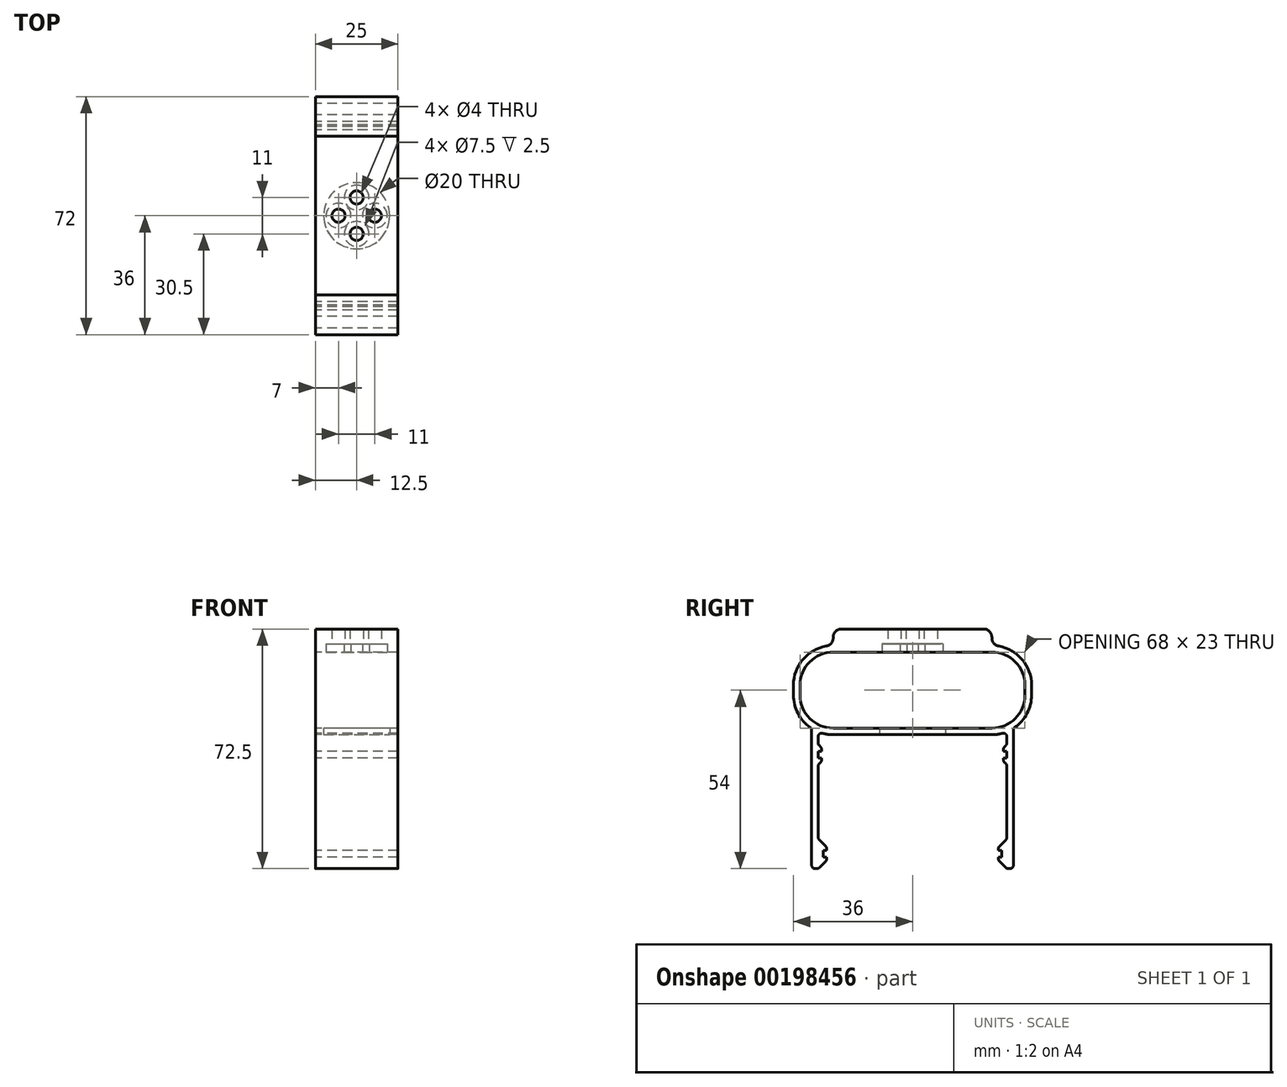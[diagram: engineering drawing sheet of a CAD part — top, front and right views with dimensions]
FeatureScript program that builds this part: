
annotation { "Feature Type Name" : "Feature", "Feature Type Description" : "" }
export const myFeature = defineFeature(function(context is Context, id is Id, definition is map)
    precondition{}
    {
        {
            var Q0;
            Q0=qCreatedBy(makeId("Right.planeOp"),FACE);
            var sketch = newSketch(context, id + "F0", { "sketchPlane" : qUnion([Q0])});
            skLineSegment(sketch, "E0.bottom", {"start": v(-24, 0) * mm, "end": v(24, 0) * mm});
            skLineSegment(sketch, "E0.top", {"start": v(-24, 23) * mm, "end": v(24, 23) * mm});
            skLineSegment(sketch, "E0.left", {"start": v(-34, 10) * mm, "end": v(-34, 13) * mm});
            skLineSegment(sketch, "E0.right", {"start": v(34, 10) * mm, "end": v(34, 13) * mm});
            skPoint(sketch, "E1.visualSharp", {"position": v(-34, 23) * mm});
            skArc(sketch, "E1.filletArc", {"start": v(-24, 23) * mm, "mid": v(-31.07, 20.07) * mm, "end": v(-34, 13) * mm});
            skPoint(sketch, "E2.visualSharp", {"position": v(-34, 0) * mm});
            skArc(sketch, "E2.filletArc", {"start": v(-34, 10) * mm, "mid": v(-31.07, 2.93) * mm, "end": v(-24, 0) * mm});
            skArc(sketch, "E3.filletArc", {"start": v(24, 0) * mm, "mid": v(31.07, 2.93) * mm, "end": v(34, 10) * mm});
            skPoint(sketch, "E4.visualSharp", {"position": v(34, 23) * mm});
            skArc(sketch, "E4.filletArc", {"start": v(34, 13) * mm, "mid": v(31.07, 20.07) * mm, "end": v(24, 23) * mm});
            skLineSegment(sketch, "E5.0", {"start": v(-24, 25) * mm, "end": v(24, 25) * mm});
            skArc(sketch, "E5.1", {"start": v(36, 13) * mm, "mid": v(32.49, 21.49) * mm, "end": v(24, 25) * mm});
            skArc(sketch, "E5.2", {"start": v(-24, 25) * mm, "mid": v(-32.49, 21.49) * mm, "end": v(-36, 13) * mm});
            skLineSegment(sketch, "E5.3", {"start": v(36, 10) * mm, "end": v(36, 13) * mm});
            skLineSegment(sketch, "E5.4", {"start": v(-36, 10) * mm, "end": v(-36, 13) * mm});
            skArc(sketch, "E5.5", {"start": v(-36, 10) * mm, "mid": v(-34.66, 4.48) * mm, "end": v(-30.92, 0.2) * mm});
            skLineSegment(sketch, "E5.6", {"start": v(-24, -2) * mm, "end": v(24, -2) * mm});
            skArc(sketch, "E5.7", {"start": v(24, -2) * mm, "mid": v(25.63, -1.89) * mm, "end": v(27.23, -1.56) * mm});
            skLineSegment(sketch, "E6", {"start": v(-28.5, -2.52) * mm, "end": v(-28.5, -4.59) * mm});
            skLineSegment(sketch, "E7", {"start": v(-28.2, -5.3) * mm, "end": v(-27.8, -5.7) * mm});
            skLineSegment(sketch, "E8", {"start": v(-27.5, -6.41) * mm, "end": v(-27.5, -7) * mm});
            skLineSegment(sketch, "E9", {"start": v(-27.5, -7) * mm, "end": v(-28.5, -7) * mm});
            skLineSegment(sketch, "E10", {"start": v(-28.5, -7) * mm, "end": v(-28.5, -9) * mm});
            skLineSegment(sketch, "E11", {"start": v(-28.5, -9) * mm, "end": v(-27.5, -9) * mm});
            skLineSegment(sketch, "E12", {"start": v(-27.5, -9) * mm, "end": v(-27.5, -9.59) * mm});
            skLineSegment(sketch, "E13", {"start": v(-27.8, -10.3) * mm, "end": v(-28.2, -10.7) * mm});
            skLineSegment(sketch, "E14", {"start": v(-28.5, -11.41) * mm, "end": v(-28.5, -33.09) * mm});
            skLineSegment(sketch, "E15", {"start": v(-28.2, -33.8) * mm, "end": v(-26.3, -35.7) * mm});
            skLineSegment(sketch, "E16", {"start": v(-26, -36.41) * mm, "end": v(-26, -37) * mm});
            skLineSegment(sketch, "E17", {"start": v(-26, -37) * mm, "end": v(-27, -37) * mm});
            skLineSegment(sketch, "E18", {"start": v(-27, -37) * mm, "end": v(-27, -39) * mm});
            skLineSegment(sketch, "E19", {"start": v(-27, -39) * mm, "end": v(-26, -39) * mm});
            skLineSegment(sketch, "E20", {"start": v(-26, -39) * mm, "end": v(-26, -39.59) * mm});
            skLineSegment(sketch, "E21", {"start": v(-26.3, -40.3) * mm, "end": v(-28.2, -42.2) * mm});
            skLineSegment(sketch, "E22", {"start": v(-28.91, -42.5) * mm, "end": v(-29.5, -42.5) * mm});
            skLineSegment(sketch, "E23", {"start": v(-30.5, -41.5) * mm, "end": v(-30.5, -0.62) * mm});
            skLineSegment(sketch, "E24.MirrorCS", {"start": v(30.5, -41.5) * mm, "end": v(30.5, -0.62) * mm});
            skLineSegment(sketch, "E25.MirrorCS", {"start": v(28.5, -2.52) * mm, "end": v(28.5, -4.59) * mm});
            skLineSegment(sketch, "E26.MirrorCS", {"start": v(28.2, -5.3) * mm, "end": v(27.8, -5.7) * mm});
            skLineSegment(sketch, "E27.MirrorCS", {"start": v(27.5, -6.41) * mm, "end": v(27.5, -7) * mm});
            skLineSegment(sketch, "E28.MirrorCS", {"start": v(27.5, -7) * mm, "end": v(28.5, -7) * mm});
            skLineSegment(sketch, "E29.MirrorCS", {"start": v(28.5, -7) * mm, "end": v(28.5, -9) * mm});
            skLineSegment(sketch, "E30.MirrorCS", {"start": v(28.5, -9) * mm, "end": v(27.5, -9) * mm});
            skLineSegment(sketch, "E31.MirrorCS", {"start": v(27.5, -9) * mm, "end": v(27.5, -9.59) * mm});
            skLineSegment(sketch, "E32.MirrorCS", {"start": v(27.8, -10.3) * mm, "end": v(28.2, -10.7) * mm});
            skLineSegment(sketch, "E33.MirrorCS", {"start": v(28.5, -11.41) * mm, "end": v(28.5, -33.09) * mm});
            skLineSegment(sketch, "E34.MirrorCS", {"start": v(28.2, -33.8) * mm, "end": v(26.3, -35.7) * mm});
            skLineSegment(sketch, "E35.MirrorCS", {"start": v(26, -36.41) * mm, "end": v(26, -37) * mm});
            skLineSegment(sketch, "E36.MirrorCS", {"start": v(26, -37) * mm, "end": v(27, -37) * mm});
            skLineSegment(sketch, "E37.MirrorCS", {"start": v(27, -37) * mm, "end": v(27, -39) * mm});
            skLineSegment(sketch, "E38.MirrorCS", {"start": v(26, -39) * mm, "end": v(26, -39.59) * mm});
            skLineSegment(sketch, "E39.MirrorCS", {"start": v(26.3, -40.3) * mm, "end": v(28.2, -42.2) * mm});
            skLineSegment(sketch, "E40.MirrorCS", {"start": v(28.91, -42.5) * mm, "end": v(29.5, -42.5) * mm});
            skLineSegment(sketch, "E41.MirrorCS", {"start": v(27, -39) * mm, "end": v(26, -39) * mm});
            skArc(sketch, "E42.trimOffspring", {"start": v(-27.23, -1.56) * mm, "mid": v(-25.63, -1.89) * mm, "end": v(-24, -2) * mm});
            skArc(sketch, "E43.trimOffspring", {"start": v(30.92, 0.2) * mm, "mid": v(34.66, 4.48) * mm, "end": v(36, 10) * mm});
            skPoint(sketch, "E44.visualSharp", {"position": v(-28.5, -1.12) * mm});
            skArc(sketch, "E44.filletArc", {"start": v(-27.23, -1.56) * mm, "mid": v(-28.1, -1.72) * mm, "end": v(-28.5, -2.52) * mm});
            skPoint(sketch, "E45.visualSharp", {"position": v(-30.5, -0.09) * mm});
            skArc(sketch, "E45.filletArc", {"start": v(-30.5, -0.62) * mm, "mid": v(-30.61, -0.16) * mm, "end": v(-30.92, 0.2) * mm});
            skPoint(sketch, "E46.visualSharp", {"position": v(28.5, -1.12) * mm});
            skArc(sketch, "E46.filletArc", {"start": v(28.5, -2.52) * mm, "mid": v(28.1, -1.72) * mm, "end": v(27.23, -1.56) * mm});
            skPoint(sketch, "E47.visualSharp", {"position": v(30.5, -0.09) * mm});
            skArc(sketch, "E47.filletArc", {"start": v(30.92, 0.2) * mm, "mid": v(30.61, -0.16) * mm, "end": v(30.5, -0.62) * mm});
            skPoint(sketch, "E48.visualSharp", {"position": v(-28.5, -5) * mm});
            skArc(sketch, "E48.filletArc", {"start": v(-28.5, -4.59) * mm, "mid": v(-28.42, -4.97) * mm, "end": v(-28.2, -5.3) * mm});
            skPoint(sketch, "E49.visualSharp", {"position": v(-27.5, -6) * mm});
            skArc(sketch, "E49.filletArc", {"start": v(-27.5, -6.41) * mm, "mid": v(-27.58, -6.03) * mm, "end": v(-27.8, -5.7) * mm});
            skPoint(sketch, "E50.visualSharp", {"position": v(-27.5, -10) * mm});
            skArc(sketch, "E50.filletArc", {"start": v(-27.8, -10.3) * mm, "mid": v(-27.58, -9.97) * mm, "end": v(-27.5, -9.59) * mm});
            skPoint(sketch, "E51.visualSharp", {"position": v(-28.5, -11) * mm});
            skArc(sketch, "E51.filletArc", {"start": v(-28.2, -10.7) * mm, "mid": v(-28.42, -11.03) * mm, "end": v(-28.5, -11.41) * mm});
            skPoint(sketch, "E52.visualSharp", {"position": v(28.5, -5) * mm});
            skArc(sketch, "E52.filletArc", {"start": v(28.2, -5.3) * mm, "mid": v(28.42, -4.97) * mm, "end": v(28.5, -4.59) * mm});
            skPoint(sketch, "E53.visualSharp", {"position": v(27.5, -6) * mm});
            skArc(sketch, "E53.filletArc", {"start": v(27.8, -5.7) * mm, "mid": v(27.58, -6.03) * mm, "end": v(27.5, -6.41) * mm});
            skPoint(sketch, "E54.visualSharp", {"position": v(27.5, -10) * mm});
            skArc(sketch, "E54.filletArc", {"start": v(27.5, -9.59) * mm, "mid": v(27.58, -9.97) * mm, "end": v(27.8, -10.3) * mm});
            skPoint(sketch, "E55.visualSharp", {"position": v(28.5, -11) * mm});
            skArc(sketch, "E55.filletArc", {"start": v(28.5, -11.41) * mm, "mid": v(28.42, -11.03) * mm, "end": v(28.2, -10.7) * mm});
            skPoint(sketch, "E56.visualSharp", {"position": v(28.5, -33.5) * mm});
            skArc(sketch, "E56.filletArc", {"start": v(28.2, -33.8) * mm, "mid": v(28.42, -33.47) * mm, "end": v(28.5, -33.09) * mm});
            skPoint(sketch, "E57.visualSharp", {"position": v(26, -36) * mm});
            skArc(sketch, "E57.filletArc", {"start": v(26.3, -35.7) * mm, "mid": v(26.08, -36.03) * mm, "end": v(26, -36.41) * mm});
            skPoint(sketch, "E58.visualSharp", {"position": v(26, -40) * mm});
            skArc(sketch, "E58.filletArc", {"start": v(26, -39.59) * mm, "mid": v(26.08, -39.97) * mm, "end": v(26.3, -40.3) * mm});
            skPoint(sketch, "E59.visualSharp", {"position": v(28.5, -42.5) * mm});
            skArc(sketch, "E59.filletArc", {"start": v(28.2, -42.2) * mm, "mid": v(28.53, -42.42) * mm, "end": v(28.91, -42.5) * mm});
            skPoint(sketch, "E60.visualSharp", {"position": v(30.5, -42.5) * mm});
            skArc(sketch, "E60.filletArc", {"start": v(29.5, -42.5) * mm, "mid": v(30.2, -42.2) * mm, "end": v(30.5, -41.5) * mm});
            skPoint(sketch, "E61.visualSharp", {"position": v(-26, -40) * mm});
            skArc(sketch, "E61.filletArc", {"start": v(-26.3, -40.3) * mm, "mid": v(-26.08, -39.97) * mm, "end": v(-26, -39.59) * mm});
            skPoint(sketch, "E62.visualSharp", {"position": v(-26, -36) * mm});
            skArc(sketch, "E62.filletArc", {"start": v(-26, -36.41) * mm, "mid": v(-26.08, -36.03) * mm, "end": v(-26.3, -35.7) * mm});
            skPoint(sketch, "E63.visualSharp", {"position": v(-28.5, -33.5) * mm});
            skArc(sketch, "E63.filletArc", {"start": v(-28.5, -33.09) * mm, "mid": v(-28.42, -33.47) * mm, "end": v(-28.2, -33.8) * mm});
            skPoint(sketch, "E64.visualSharp", {"position": v(-28.5, -42.5) * mm});
            skArc(sketch, "E64.filletArc", {"start": v(-28.91, -42.5) * mm, "mid": v(-28.53, -42.42) * mm, "end": v(-28.2, -42.2) * mm});
            skPoint(sketch, "E65.visualSharp", {"position": v(-30.5, -42.5) * mm});
            skArc(sketch, "E65.filletArc", {"start": v(-30.5, -41.5) * mm, "mid": v(-30.2, -42.2) * mm, "end": v(-29.5, -42.5) * mm});
            skSolve(sketch);
        }
        {
            var Q0;
            Q0=qSketchRegion(id+"F0",true);
            extrude(context, id + "F1", {"entities" : qUnion([Q0]), "depth" : 25 * mm});
        }
        {
            var Q0;
            Q0=makeQuery(id+"F1.opExtrude","SWEPT_FACE",FACE,{"disambiguationData":[OSD([sQuery(id+"F0.wireOp",EDGE,"E0.top")])]});
            var sketch = newSketch(context, id + "F2", { "sketchPlane" : qUnion([Q0])});
            skCircle(sketch, "E66", {"center": v(7, 0) * mm, "radius": 2 * mm});
            skCircle(sketch, "E67.1.0", {"center": v(12.5, -5.5) * mm, "radius": 2 * mm});
            skCircle(sketch, "E67.2.0", {"center": v(18, 0) * mm, "radius": 2 * mm});
            skCircle(sketch, "E67.3.0", {"center": v(12.5, 5.5) * mm, "radius": 2 * mm});
            skPoint(sketch, "E67.center", {"position": v(12.5, 0) * mm});
            skLineSegment(sketch, "E68", {"start": v(0, 0) * mm, "end": v(25, 0) * mm, "construction": true});
            skSolve(sketch);
        }
        {
            var Q0;
            Q0=makeQuery(id+"F1.opExtrude","SWEPT_FACE",FACE,{"disambiguationData":[OSD([sQuery(id+"F0.wireOp",EDGE,"E5.0")])]});
            extrude(context, id + "F3", {"entities" : qUnion([Q0]), "operationType" : NewBodyOperationType.ADD, "depth" : 5 * mm});
        }
        {
            var Q0;
            Q0=qSketchRegion(id+"F2",true);
            extrude(context, id + "F4", {"entities" : qUnion([Q0]), "operationType" : NewBodyOperationType.REMOVE, "endBound" : BoundingType.THROUGH_ALL, "oppositeDirection" : true, "depth" : 25 * mm});
        }
        {
            var Q0;
            Q0=makeQuery(id+"F1.opExtrude","SWEPT_FACE",FACE,{"disambiguationData":[OSD([sQuery(id+"F0.wireOp",EDGE,"E0.top")])]});
            var sketch = newSketch(context, id + "F5", { "sketchPlane" : qUnion([Q0])});
            skPoint(sketch, "E69", {"position": v(12.5, -5.5) * mm});
            skPoint(sketch, "E70", {"position": v(12.5, 5.5) * mm});
            skPoint(sketch, "E71", {"position": v(7, 0) * mm});
            skPoint(sketch, "E72", {"position": v(18, 0) * mm});
            skSolve(sketch);
        }
        {
            var Q0;
            Q0=sQuery(id+"F5.wireOp",VERTEX,"E69");
            var Q1;
            Q1=sQuery(id+"F5.wireOp",VERTEX,"E71");
            var Q2;
            Q2=sQuery(id+"F5.wireOp",VERTEX,"E72");
            var Q3;
            Q3=sQuery(id+"F5.wireOp",VERTEX,"E70");
            var Q4;
            Q4=makeQuery(id+"F1.opExtrude","SWEPT_BODY",BODY,{"disambiguationData":[OSD([sQuery(id+"F0.wireOp",EDGE,"E0.bottom"),sQuery(id+"F0.wireOp",EDGE,"E0.top"),sQuery(id+"F0.wireOp",EDGE,"E1.filletArc"),sQuery(id+"F0.wireOp",EDGE,"E2.filletArc"),sQuery(id+"F0.wireOp",EDGE,"E3.filletArc"),sQuery(id+"F0.wireOp",EDGE,"E4.filletArc"),sQuery(id+"F0.wireOp",EDGE,"e41423a2-ebfb-4468-8629-81b6496931a8.0"),sQuery(id+"F0.wireOp",EDGE,"e41423a2-ebfb-4468-8629-81b6496931a8.1"),sQuery(id+"F0.wireOp",EDGE,"e41423a2-ebfb-4468-8629-81b6496931a8.2"),sQuery(id+"F0.wireOp",EDGE,"e41423a2-ebfb-4468-8629-81b6496931a8.3"),sQuery(id+"F0.wireOp",EDGE,"e41423a2-ebfb-4468-8629-81b6496931a8.5"),sQuery(id+"F0.wireOp",EDGE,"jOwyFaz2-FClo-lyoE-OEFV-Swf1H60Ilg78"),sQuery(id+"F0.wireOp",EDGE,"UlCknQYV-mY9B-t4R5-7gRI-73dWkxDY4DMy"),sQuery(id+"F0.wireOp",EDGE,"DvKAl2Jq-LLt8-zbq4-aSFj-cuOSZKTQXl5e"),sQuery(id+"F0.wireOp",EDGE,"NgJzEhDJ-QYk7-GHVG-krLP-QBaYv62ZhdbK"),sQuery(id+"F0.wireOp",EDGE,"NsI0x6xM-M73M-cjv9-vUbN-SS34C4QLM709"),sQuery(id+"F0.wireOp",EDGE,"kbyAHR4M-evz6-4fjq-npYn-1yHfS1X5xHSp"),sQuery(id+"F0.wireOp",EDGE,"ylG7BHDF-5bN5-u6O8-TNcV-3VaRnEf41Aw4"),sQuery(id+"F0.wireOp",EDGE,"3e6d006e-de8a-4d88-b0bf-77b06e834a52.trimOffspring"),sQuery(id+"F0.wireOp",EDGE,"c045c551-d941-4a29-a602-f2893d381402.filletArc"),sQuery(id+"F0.wireOp",EDGE,"8a2ee916-e2c3-4787-b37f-4edbb8cf494e.filletArc"),sQuery(id+"F0.wireOp",EDGE,"d2fc5667-90e4-4240-8a31-059ff47e73a1.filletArc"),sQuery(id+"F0.wireOp",EDGE,"bca0e1dd-eb26-4abb-9b87-c1e40bd55cdd.filletArc"),sQuery(id+"F0.wireOp",EDGE,"bd23e3bd-3ea8-4d5f-b805-cf22bb377c5a.filletArc"),sQuery(id+"F0.wireOp",EDGE,"3abcb055-c86b-423e-898b-e811cc45f268.filletArc"),sQuery(id+"F0.wireOp",EDGE,"f26c2ede-9b26-4cee-8ef5-d49a595beb8a.filletArc"),sQuery(id+"F0.wireOp",EDGE,"b55cadc2-29c4-4d06-ad0c-f61fb8679a1b.filletArc"),sQuery(id+"F0.wireOp",EDGE,"89f69a5c-81cd-4382-904c-2ff434b634c6.filletArc"),sQuery(id+"F0.wireOp",EDGE,"e703850d-a559-47ff-86cd-c3c569d74d68.filletArc"),sQuery(id+"F0.wireOp",EDGE,"20a132c9-6f9d-438b-8a7f-ce58f982453a.filletArc"),sQuery(id+"F0.wireOp",EDGE,"ee91e716-4c16-4ef9-bcf7-48daeec8f5f5.filletArc"),sQuery(id+"F0.wireOp",EDGE,"a1fe6970-631c-4b55-98fe-c7cfef8980630.MirrorCS"),sQuery(id+"F0.wireOp",EDGE,"a1fe6970-631c-4b55-98fe-c7cfef8980631.MirrorCS"),sQuery(id+"F0.wireOp",EDGE,"a1fe6970-631c-4b55-98fe-c7cfef8980632.MirrorCS"),sQuery(id+"F0.wireOp",EDGE,"a1fe6970-631c-4b55-98fe-c7cfef8980633.MirrorCS"),sQuery(id+"F0.wireOp",EDGE,"a1fe6970-631c-4b55-98fe-c7cfef8980634.MirrorCS"),sQuery(id+"F0.wireOp",EDGE,"a1fe6970-631c-4b55-98fe-c7cfef8980635.MirrorCS"),sQuery(id+"F0.wireOp",EDGE,"a1fe6970-631c-4b55-98fe-c7cfef8980636.MirrorCS"),sQuery(id+"F0.wireOp",EDGE,"a1fe6970-631c-4b55-98fe-c7cfef8980637.MirrorCS"),sQuery(id+"F0.wireOp",EDGE,"a1fe6970-631c-4b55-98fe-c7cfef8980638.MirrorCS"),sQuery(id+"F0.wireOp",EDGE,"a1fe6970-631c-4b55-98fe-c7cfef8980639.MirrorCS"),sQuery(id+"F0.wireOp",EDGE,"a1fe6970-631c-4b55-98fe-c7cfef89806310.MirrorCS"),sQuery(id+"F0.wireOp",EDGE,"a1fe6970-631c-4b55-98fe-c7cfef89806311.MirrorCS"),sQuery(id+"F0.wireOp",EDGE,"a1fe6970-631c-4b55-98fe-c7cfef89806312.MirrorCS"),sQuery(id+"F0.wireOp",EDGE,"a1fe6970-631c-4b55-98fe-c7cfef89806313.MirrorCS"),sQuery(id+"F0.wireOp",EDGE,"a1fe6970-631c-4b55-98fe-c7cfef89806314.MirrorCS"),sQuery(id+"F0.wireOp",EDGE,"a1fe6970-631c-4b55-98fe-c7cfef89806315.MirrorCS"),sQuery(id+"F0.wireOp",EDGE,"a1fe6970-631c-4b55-98fe-c7cfef89806316.MirrorCS"),sQuery(id+"F0.wireOp",EDGE,"a1fe6970-631c-4b55-98fe-c7cfef89806323.MirrorCS"),sQuery(id+"F0.wireOp",EDGE,"a1fe6970-631c-4b55-98fe-c7cfef89806329.MirrorCS"),sQuery(id+"F0.wireOp",EDGE,"a1fe6970-631c-4b55-98fe-c7cfef89806334.MirrorCS"),sQuery(id+"F0.wireOp",EDGE,"b78078e7-dd9c-48c8-ba60-cbfb4d4adaee.trimOffspring")])]});
            hole(context, id + "F6", {"style" : HoleStyle.C_BORE, "endStyle" : HoleEndStyle.THROUGH, "holeDiameter" : 4 * mm, "cBoreDiameter" : 7.5 * mm, "cBoreDepth" : 2.5 * mm, "locations" : qUnion([Q0, Q1, Q2, Q3]), "scope" : qUnion([Q4]), "isTappedThrough" : true});
        }
        {
            var Q0;
            Q0=makeQuery(id+"F1.opExtrude","SWEPT_FACE",FACE,{"disambiguationData":[OSD([sQuery(id+"F0.wireOp",EDGE,"E5.6")])]});
            var sketch = newSketch(context, id + "F7", { "sketchPlane" : qUnion([Q0])});
            skLineSegment(sketch, "E73", {"start": v(12.5, 5.5) * mm, "end": v(12.5, -5.5) * mm, "construction": true});
            skCircle(sketch, "E74", {"center": v(12.5, 0) * mm, "radius": 10 * mm});
            skSolve(sketch);
        }
        {
            var Q0;
            Q0 = qSketchRegion(id + "F7", true);
            extrude(context, id + "F8", {"entities" : qUnion([Q0]), "operationType" : NewBodyOperationType.REMOVE, "endBound" : BoundingType.UP_TO_NEXT, "oppositeDirection" : true, "depth" : 25 * mm});
        }
        {
            var Q0;
            {var subQ0=sQuery(id+"F0.wireOp",EDGE,"E5.2");var subQ1=sQuery(id+"F0.wireOp",EDGE,"E5.0");Q0=makeQuery(id+"F3.boolean.opBoolean","MERGE",EDGE,{"derivedFrom":[makeQuery(id+"F1.opExtrude","SWEPT_EDGE",EDGE,{"disambiguationData":[OSD([subQ1,subQ0])]}),makeQuery(id+"F3.opExtrude","CAP_EDGE",EDGE,{"disambiguationData":[OSD([subQ1,subQ0])],"isStart":true})]});}
            var Q1;
            {var subQ0=sQuery(id+"F0.wireOp",EDGE,"E5.1");var subQ1=sQuery(id+"F0.wireOp",EDGE,"E5.0");Q1=makeQuery(id+"F3.boolean.opBoolean","MERGE",EDGE,{"derivedFrom":[makeQuery(id+"F1.opExtrude","SWEPT_EDGE",EDGE,{"disambiguationData":[OSD([subQ1,subQ0])]}),makeQuery(id+"F3.opExtrude","CAP_EDGE",EDGE,{"disambiguationData":[OSD([subQ1,subQ0])],"isStart":true})]});}
            var Q2;
            Q2=makeQuery(id+"F3.opExtrude","CAP_EDGE",EDGE,{"disambiguationData":[OSD([sQuery(id+"F0.wireOp",EDGE,"E5.0"),sQuery(id+"F0.wireOp",EDGE,"E5.1")])],"isStart":false});
            var Q3;
            Q3=makeQuery(id+"F3.opExtrude","CAP_EDGE",EDGE,{"disambiguationData":[OSD([sQuery(id+"F0.wireOp",EDGE,"E5.0"),sQuery(id+"F0.wireOp",EDGE,"E5.2")])],"isStart":false});
            fillet(context, id + "F9", {"entities" : qUnion([Q0, Q1, Q2, Q3]), "radius" : 2.5 * mm, "tangentPropagation" : true, "allowEdgeOverflow" : false});
        }
    });
